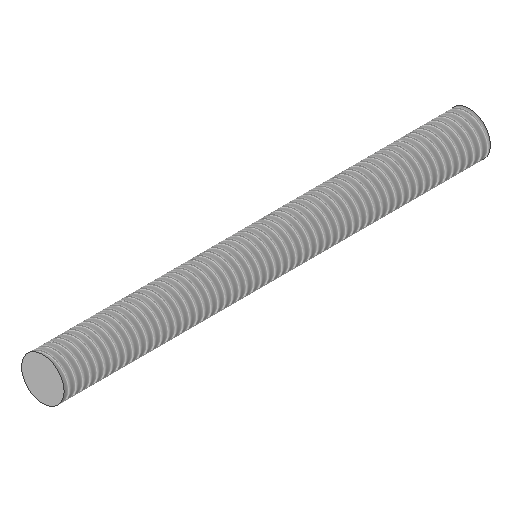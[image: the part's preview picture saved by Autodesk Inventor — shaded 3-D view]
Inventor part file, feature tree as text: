
AUTODESK INVENTOR PART (.ipt)
format: ipt  version: 2025.1 (Build 291241000, 241)  size: 140,288 bytes
history: native  units: mm
features: other x1, extrude x1, thread x1, sketch x1
ambient origin geometry x8: Origin, YZ Plane, XZ Plane, XY Plane, X Axis, Y Axis, Z Axis, Center Point
bodies: Body1 (feature_tree)
feature tree (4):
  other  "Bryła1"
  extrude  "Wyciągnięcie proste1"  Depth=3.0mm
  thread  "Gwint1"
  sketch  "Szkic1"
